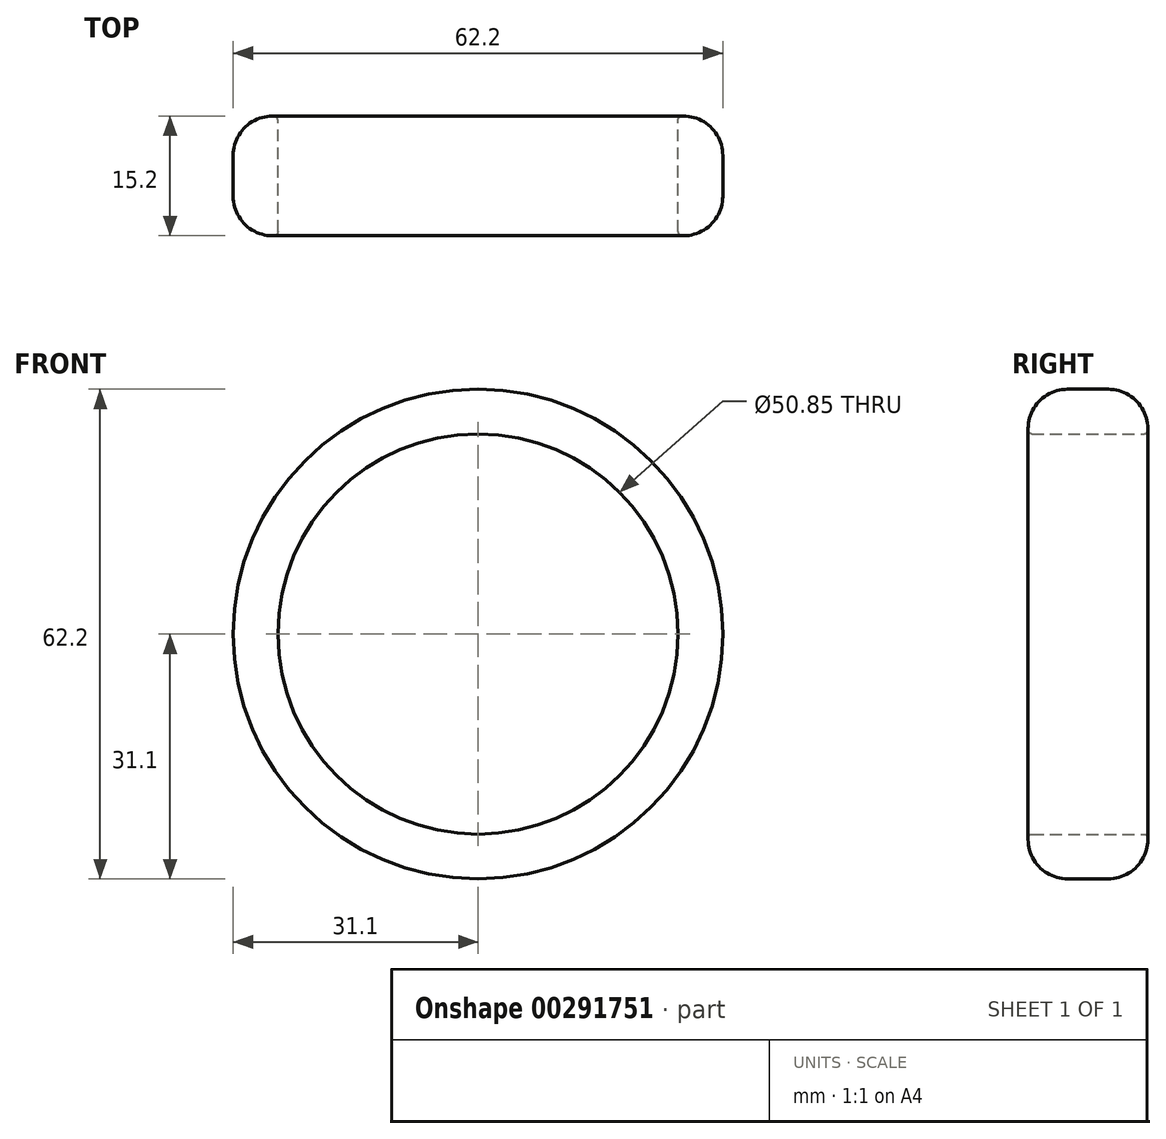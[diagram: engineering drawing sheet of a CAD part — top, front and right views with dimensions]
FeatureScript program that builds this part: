
annotation { "Feature Type Name" : "Feature", "Feature Type Description" : "" }
export const myFeature = defineFeature(function(context is Context, id is Id, definition is map)
    precondition{}
    {
        {
            var Q0;
            Q0=qCreatedBy(makeId("Front.planeOp"),FACE);
            var sketch = newSketch(context, id + "F0", { "sketchPlane" : qUnion([Q0])});
            skCircle(sketch, "E0", {"center": v(0, 0) * mm, "radius": 25.42 * mm});
            skCircle(sketch, "E1", {"center": v(0, 0) * mm, "radius": 31.1 * mm});
            skSolve(sketch);
        }
        {
            var Q0;
            Q0=makeQuery(id+"F0.imprint","IMPRINT",FACE,{"disambiguationData":[TD([[makeQuery(id+"F0.imprint","IMPRINT",EDGE,{"derivedFrom":sQuery(id+"F0.wireOp",EDGE,"E0")}),-1.0]])]});
            extrude(context, id + "F1", {"entities" : qUnion([Q0]), "depth" : 15.2 * mm, "offsetDistance" : 25 * mm, "symmetric" : true});
        }
        {
            var Q0;
            Q0=makeQuery(id+"F1.opExtrude","SWEPT_FACE",FACE,{"disambiguationData":[OSD([sQuery(id+"F0.wireOp",EDGE,"E1")])]});
            fillet(context, id + "F2", {"entities" : qUnion([Q0]), "tangentPropagation" : true, "radius" : 5 * mm, "defaultsChanged" : false, "vertexSettings" : [], "allowEdgeOverflow" : false});
        }
        {
            var Q0;
            Q0=makeQuery(id+"F1.opExtrude","SWEPT_FACE",FACE,{"disambiguationData":[OSD([sQuery(id+"F0.wireOp",EDGE,"E0")])]});
            fillet(context, id + "F3", {"entities" : qUnion([Q0]), "tangentPropagation" : true, "radius" : 0.5 * mm, "defaultsChanged" : true, "vertexSettings" : [], "allowEdgeOverflow" : false});
        }
    });
